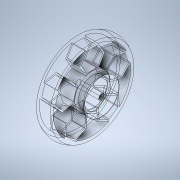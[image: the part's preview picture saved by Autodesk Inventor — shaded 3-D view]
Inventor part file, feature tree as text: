
AUTODESK INVENTOR PART (.ipt)
format: ipt  version: 2020 (Build 240168000, 168)  size: 439,808 bytes
history: native  units: in
note: dims shown in document units (in); Inventor stores cm internally (conversion verified against a paired STEP export)
features: sketch x4, extrude x2, revolve x2, projected_geometry x1
ambient origin geometry x8: Origin, YZ Plane, XZ Plane, XY Plane, X Axis, Y Axis, Z Axis, Center Point
bodies: Solid1 (feature_tree)
feature tree (9):
  extrude  "Extrusion1"  Depth=0.0394in
  sketch  "Sketch3"  dims[d6=0.7087in d7=0.1969in]
  revolve  "Revolution1"  [1 undecoded]
  extrude  "Extrusion2"  Depth=0.1969in
  revolve  "Revolution2"  [1 undecoded]
  sketch  "Sketch1"  dims[d0=0.1181in d1=0.0394in]
  sketch  "Sketch2"  dims[d3=1.6929in d4=0.1181in]
  projected_geometry  "Projected Loop1"
  sketch  "Sketch4"  dims[d8=0.0in d9=1.6929in d10=0.063in d11=0.0315in d16=0.2756in d17=0.0in d19=360.0deg d20=0.0984in d24=0.0394in d25=90.0deg d26=45.0deg d28=0.0079in d29=1.9685in d31=360.0deg]
note: 2 required parameter values undecoded (feature->parameter linkage not recoverable at this tier; creation-order binding heuristic only, values carry confidence <= 0.55)
